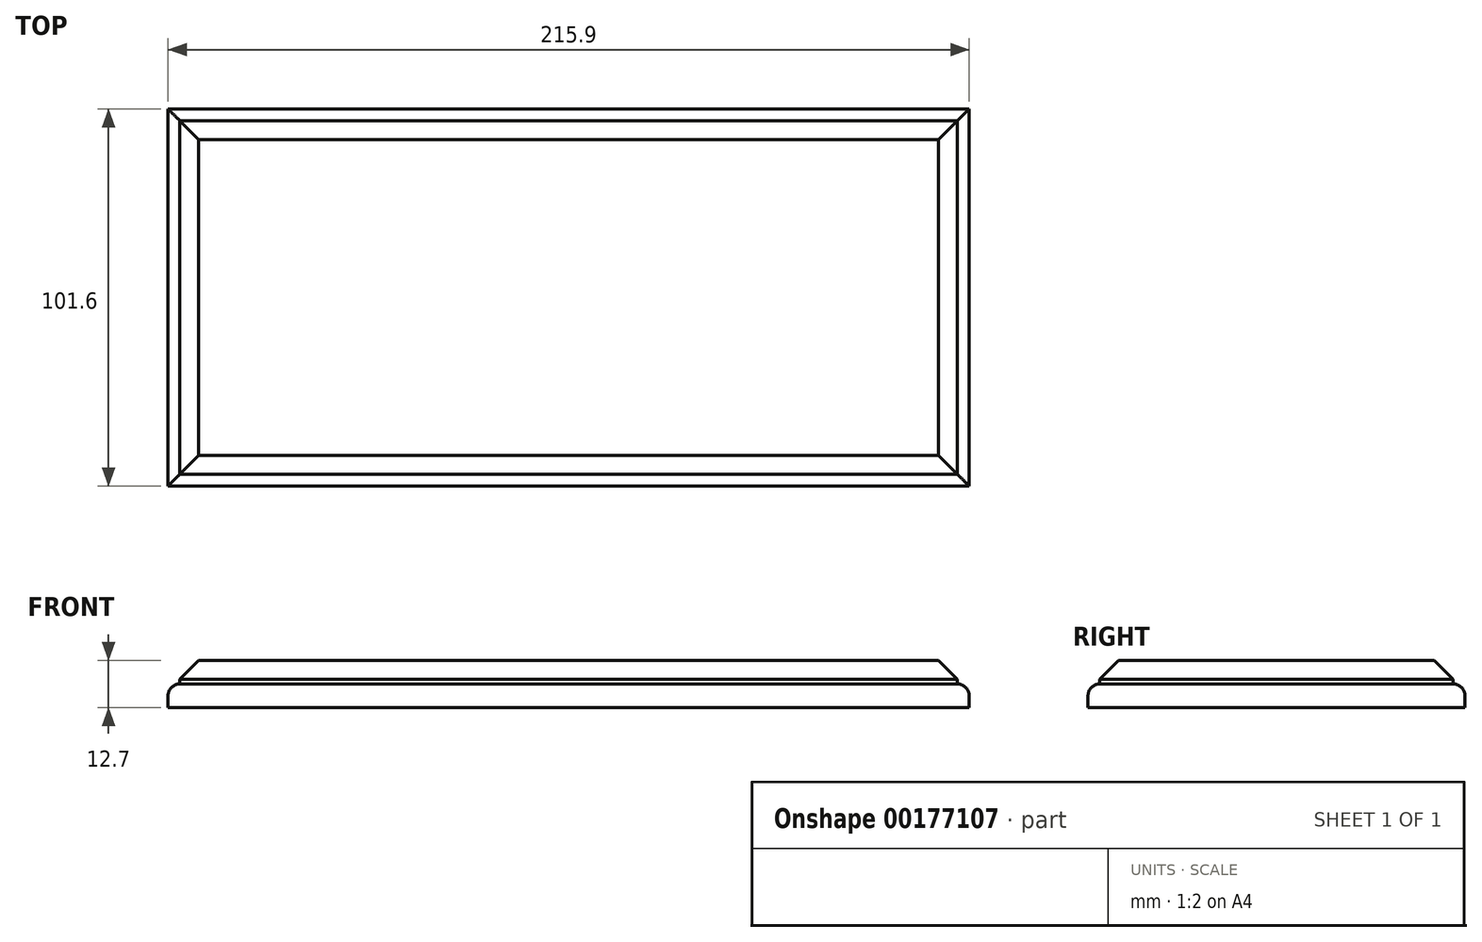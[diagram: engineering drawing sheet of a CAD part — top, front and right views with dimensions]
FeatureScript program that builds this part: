
annotation { "Feature Type Name" : "Feature", "Feature Type Description" : "" }
export const myFeature = defineFeature(function(context is Context, id is Id, definition is map)
    precondition{}
    {
        {
            var Q0;
            Q0=qCreatedBy(makeId("Top.planeOp"),FACE);
            var sketch = newSketch(context, id + "F0", { "sketchPlane" : qUnion([Q0])});
            skLineSegment(sketch, "E0.bottom", {"start": v(-124.81, 49.96) * mm, "end": v(91.09, 49.96) * mm});
            skLineSegment(sketch, "E0.top", {"start": v(-124.81, -51.64) * mm, "end": v(91.09, -51.64) * mm});
            skLineSegment(sketch, "E0.left", {"start": v(-124.81, 49.96) * mm, "end": v(-124.81, -51.64) * mm});
            skLineSegment(sketch, "E0.right", {"start": v(91.09, 49.96) * mm, "end": v(91.09, -51.64) * mm});
            skSolve(sketch);
        }
        {
            var Q0;
            Q0=makeQuery(id+"F0.imprint","IMPRINT",FACE,{"disambiguationData":[TD([[makeQuery(id+"F0.imprint","IMPRINT",EDGE,{"derivedFrom":sQuery(id+"F0.wireOp",EDGE,"E0.bottom")}),-1.0]])]});
            extrude(context, id + "F1", {"entities" : qUnion([Q0]), "depth" : 6.35 * mm});
        }
        {
            var Q0;
            Q0=makeQuery(id+"F1.opExtrude","CAP_FACE",FACE,{"disambiguationData":[OSD([sQuery(id+"F0.wireOp",EDGE,"E0.bottom"),sQuery(id+"F0.wireOp",EDGE,"E0.top"),sQuery(id+"F0.wireOp",EDGE,"E0.left"),sQuery(id+"F0.wireOp",EDGE,"E0.right")])],"isStart":false});
            fillet(context, id + "F2", {"entities" : qUnion([Q0]), "radius" : 3.17 * mm, "tangentPropagation" : true, "allowEdgeOverflow" : false});
        }
        {
            var Q0;
            Q0=makeQuery(id+"F1.opExtrude","CAP_FACE",FACE,{"disambiguationData":[OSD([sQuery(id+"F0.wireOp",EDGE,"E0.bottom"),sQuery(id+"F0.wireOp",EDGE,"E0.top"),sQuery(id+"F0.wireOp",EDGE,"E0.left"),sQuery(id+"F0.wireOp",EDGE,"E0.right")])],"isStart":false});
            extrude(context, id + "F3", {"entities" : qUnion([Q0]), "operationType" : NewBodyOperationType.ADD, "depth" : 6.35 * mm});
        }
        {
            var Q0;
            Q0=makeQuery(id+"F3.opExtrude","CAP_FACE",FACE,{"disambiguationData":[OSD([sQuery(id+"F0.wireOp",EDGE,"E0.bottom"),sQuery(id+"F0.wireOp",EDGE,"E0.top"),sQuery(id+"F0.wireOp",EDGE,"E0.left"),sQuery(id+"F0.wireOp",EDGE,"E0.right")])],"isStart":false});
            chamfer(context, id + "F4", {"entities" : qUnion([Q0]), "width" : 5.08 * mm, "tangentPropagation" : true});
        }
    });
